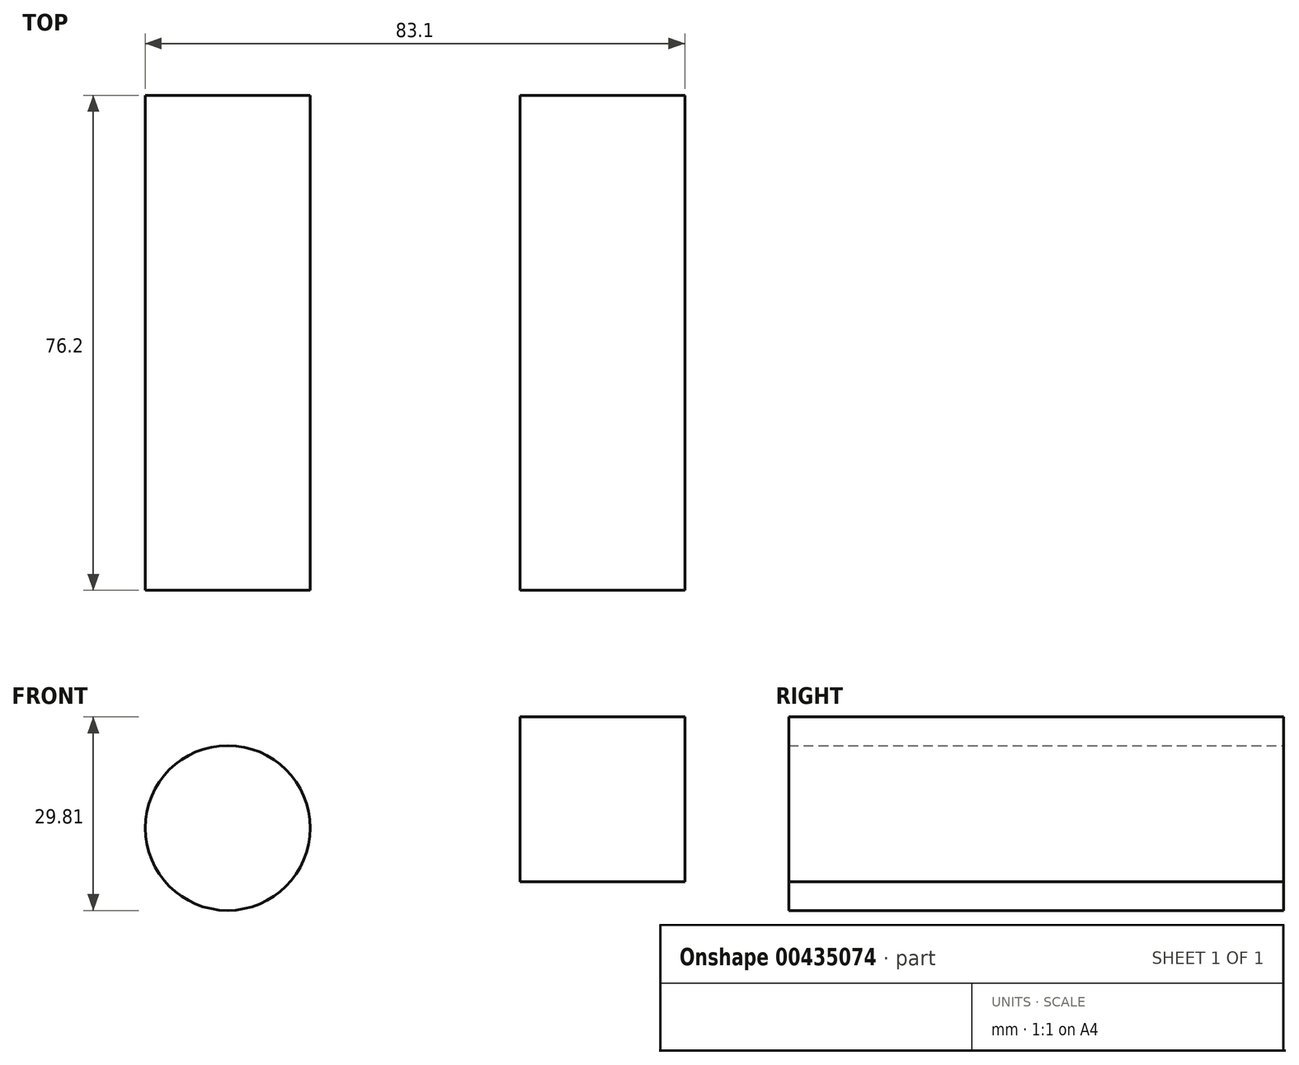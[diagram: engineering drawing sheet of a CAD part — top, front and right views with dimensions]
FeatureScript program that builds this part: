
annotation { "Feature Type Name" : "Feature", "Feature Type Description" : "" }
export const myFeature = defineFeature(function(context is Context, id is Id, definition is map)
    precondition{}
    {
        {
            var Q0;
            Q0=qCreatedBy(makeId("Front.planeOp"),FACE);
            var sketch = newSketch(context, id + "F0", { "sketchPlane" : qUnion([Q0])});
            skCircle(sketch, "E0", {"center": v(-44.91, 22.96) * mm, "radius": 12.7 * mm});
            skLineSegment(sketch, "E1.bottom", {"start": v(0.09, 40.07) * mm, "end": v(25.49, 40.07) * mm});
            skLineSegment(sketch, "E1.top", {"start": v(0.09, 14.67) * mm, "end": v(25.49, 14.67) * mm});
            skLineSegment(sketch, "E1.left", {"start": v(0.09, 40.07) * mm, "end": v(0.09, 14.67) * mm});
            skLineSegment(sketch, "E1.right", {"start": v(25.49, 40.07) * mm, "end": v(25.49, 14.67) * mm});
            skSolve(sketch);
        }
        {
            var Q0;
            Q0 = qSketchRegion(id + "F0", true);
            extrude(context, id + "F1", {"entities" : qUnion([Q0]), "depth" : 76.2 * mm});
        }
    });
